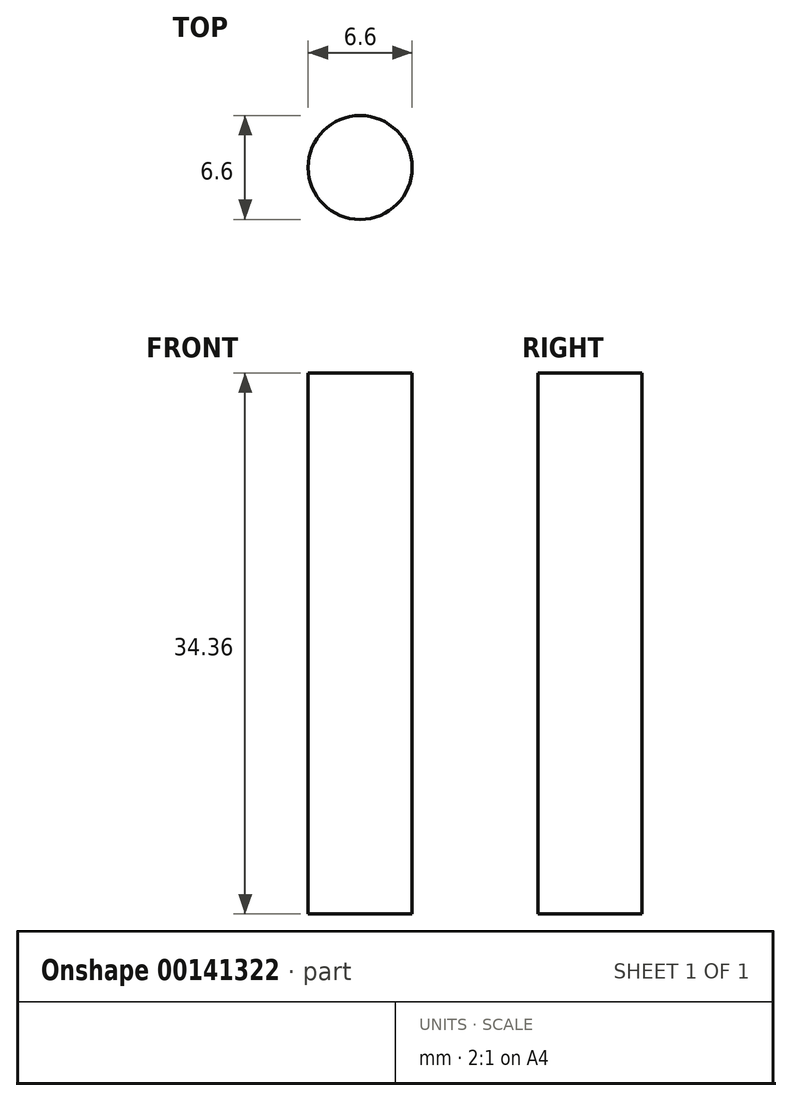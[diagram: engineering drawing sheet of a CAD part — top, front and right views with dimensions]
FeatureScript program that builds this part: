
annotation { "Feature Type Name" : "Feature", "Feature Type Description" : "" }
export const myFeature = defineFeature(function(context is Context, id is Id, definition is map)
    precondition{}
    {
        {
            var Q0;
            Q0=qCreatedBy(makeId("Right.planeOp"),FACE);
            var sketch = newSketch(context, id + "F1", { "sketchPlane" : qUnion([Q0])});
            skLineSegment(sketch, "E0", {"start": v(0, 0) * mm, "end": v(44.45, 0) * mm, "construction": true});
            skCircle(sketch, "E1", {"center": v(44.45, 0) * mm, "radius": 10.16 * mm});
            skLineSegment(sketch, "E2", {"start": v(0, 0) * mm, "end": v(0, 17.18) * mm});
            skLineSegment(sketch, "E3", {"start": v(0, 17.18) * mm, "end": v(44.45, 17.18) * mm});
            skLineSegment(sketch, "E4", {"start": v(44.45, 17.18) * mm, "end": v(44.45, 10.16) * mm});
            skLineSegment(sketch, "E5", {"start": v(44.45, 10.16) * mm, "end": v(44.45, 10.16) * mm});
            skLineSegment(sketch, "E6.MirrorCS", {"start": v(44.45, -17.18) * mm, "end": v(44.45, -10.16) * mm});
            skLineSegment(sketch, "E7.MirrorCS", {"start": v(0, -17.18) * mm, "end": v(44.45, -17.18) * mm});
            skLineSegment(sketch, "E8.MirrorCS", {"start": v(0, 0) * mm, "end": v(0, -17.18) * mm});
            skLineSegment(sketch, "E9", {"start": v(0, 17.18) * mm, "end": v(0, 36.02) * mm, "construction": true});
            skSolve(sketch);
        }
        {
            var Q0;
            Q0=makeQuery(id+"F1.imprint","IMPRINT",FACE,{"disambiguationData":[TD([[makeQuery(id+"F1.imprint","IMPRINT",EDGE,{"derivedFrom":sQuery(id+"F1.wireOp",EDGE,"E2")}),-1.0]])]});
            var Q1;
            Q1=sQuery(id+"F1.wireOp",EDGE,"E9");
            revolve(context, id + "F2", {"entities" : qUnion([Q0]), "axis" : qUnion([Q1]), "revolveType" : RevolveType.ONE_DIRECTION, "angle" : 90 * degree});
        }
        {
            var Q0;
            Q0=makeQuery(id+"F2.opRevolve","SWEPT_FACE",FACE,{"disambiguationData":[OSD([sQuery(id+"F1.wireOp",EDGE,"E7.MirrorCS")])]});
            var sketch = newSketch(context, id + "F0", { "sketchPlane" : qUnion([Q0])});
            skLineSegment(sketch, "E10.bottom", {"start": v(0, 0) * mm, "end": v(-20.32, 0) * mm});
            skLineSegment(sketch, "E10.top", {"start": v(0, -20.32) * mm, "end": v(-20.32, -20.32) * mm});
            skLineSegment(sketch, "E10.left", {"start": v(0, 0) * mm, "end": v(0, -20.32) * mm});
            skLineSegment(sketch, "E10.right", {"start": v(-20.32, 0) * mm, "end": v(-20.32, -20.32) * mm});
            skSolve(sketch);
        }
        {
            var Q0;
            Q0=makeQuery(id+"F0.imprint","IMPRINT",FACE,{"disambiguationData":[TD([[makeQuery(id+"F0.imprint","IMPRINT",EDGE,{"derivedFrom":sQuery(id+"F0.wireOp",EDGE,"E10.bottom")}),1.0]])]});
            extrude(context, id + "F3", {"entities" : qUnion([Q0]), "operationType" : NewBodyOperationType.REMOVE, "endBound" : BoundingType.THROUGH_ALL, "oppositeDirection" : true, "depth" : 25.4 * mm});
        }
        {
            var Q0;
            Q0=makeQuery(id+"F2.opRevolve","SWEPT_FACE",FACE,{"disambiguationData":[OSD([sQuery(id+"F1.wireOp",EDGE,"E7.MirrorCS")])]});
            var sketch = newSketch(context, id + "F4", { "sketchPlane" : qUnion([Q0])});
            skLineSegment(sketch, "E11", {"start": v(0, -20.32) * mm, "end": v(0, -29.21) * mm, "construction": true});
            skLineSegment(sketch, "E12", {"start": v(0, -29.21) * mm, "end": v(-7.62, -29.21) * mm, "construction": true});
            skCircle(sketch, "E13", {"center": v(-7.62, -29.21) * mm, "radius": 3.3 * mm});
            skLineSegment(sketch, "E14", {"start": v(-20.32, -20.32) * mm, "end": v(0, 0) * mm, "construction": true});
            skCircle(sketch, "E15.MirrorC", {"center": v(-29.21, -7.62) * mm, "radius": 3.3 * mm});
            skSolve(sketch);
        }
        {
            var Q0;
            Q0=makeQuery(id+"F4.imprint","IMPRINT",FACE,{"disambiguationData":[TD([[makeQuery(id+"F4.imprint","IMPRINT",EDGE,{"derivedFrom":sQuery(id+"F4.wireOp",EDGE,"E15.MirrorC")}),-1.0]])]});
            var Q1;
            Q1=makeQuery(id+"F4.imprint","IMPRINT",FACE,{"disambiguationData":[TD([[makeQuery(id+"F4.imprint","IMPRINT",EDGE,{"derivedFrom":sQuery(id+"F4.wireOp",EDGE,"E13")}),1.0]])]});
            extrude(context, id + "F5", {"entities" : qUnion([Q0, Q1]), "operationType" : NewBodyOperationType.REMOVE, "endBound" : BoundingType.THROUGH_ALL, "oppositeDirection" : true, "depth" : 25.4 * mm});
        }
    });
